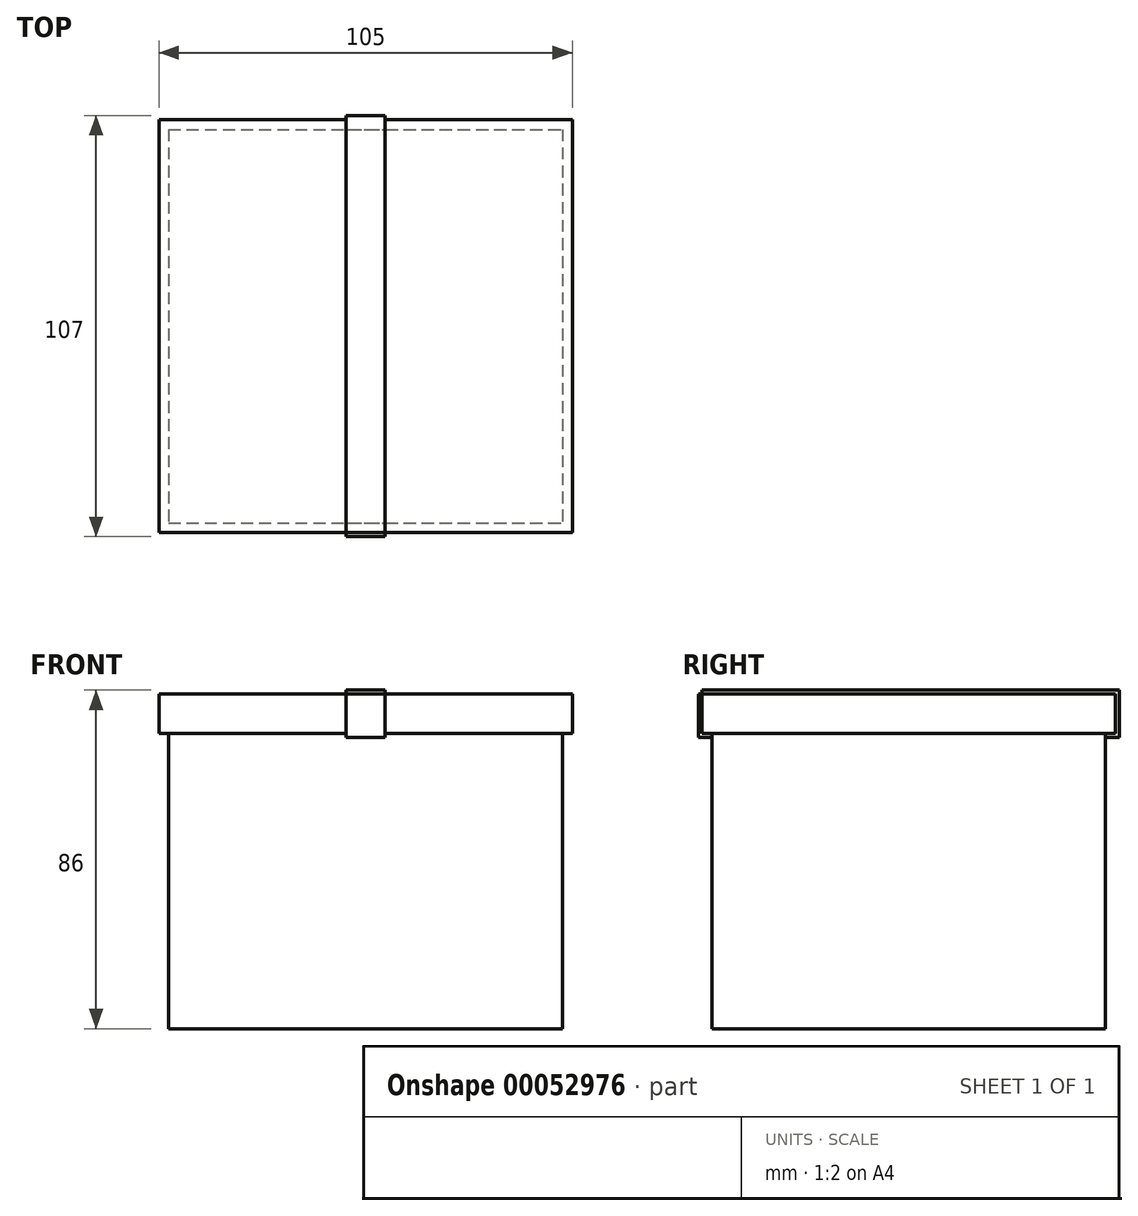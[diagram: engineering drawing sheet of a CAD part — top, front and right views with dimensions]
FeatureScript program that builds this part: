
annotation { "Feature Type Name" : "Feature", "Feature Type Description" : "" }
export const myFeature = defineFeature(function(context is Context, id is Id, definition is map)
    precondition{}
    {
        {
            var Q0;
            Q0=qCreatedBy(makeId("Top.planeOp"),FACE);
            var sketch = newSketch(context, id + "F0", { "sketchPlane" : qUnion([Q0])});
            skLineSegment(sketch, "E0.bottom", {"start": v(-50.02, 49.97) * mm, "end": v(49.98, 49.97) * mm});
            skLineSegment(sketch, "E0.top", {"start": v(-50.02, -50.03) * mm, "end": v(49.98, -50.03) * mm});
            skLineSegment(sketch, "E0.left", {"start": v(-50.02, 49.97) * mm, "end": v(-50.02, -50.03) * mm});
            skLineSegment(sketch, "E0.right", {"start": v(49.98, 49.97) * mm, "end": v(49.98, -50.03) * mm});
            skSolve(sketch);
        }
        {
            var Q0;
            Q0 = qSketchRegion(id + "F0", true);
            var Q1;
            Q1=makeQuery(id+"F0.imprint","IMPRINT",FACE,{"disambiguationData":[TD([[makeQuery(id+"F0.imprint","IMPRINT",EDGE,{"derivedFrom":sQuery(id+"F0.wireOp",EDGE,"E0.bottom")}),-1.0]])]});
            extrude(context, id + "F1", {"entities" : qUnion([Q0, Q1]), "depth" : 75 * mm});
        }
        {
            var Q0;
            Q0=makeQuery(id+"F1.opExtrude","CAP_FACE",FACE,{"disambiguationData":[OSD([sQuery(id+"F0.wireOp",EDGE,"E0.bottom"),sQuery(id+"F0.wireOp",EDGE,"E0.top"),sQuery(id+"F0.wireOp",EDGE,"E0.left"),sQuery(id+"F0.wireOp",EDGE,"E0.right")])],"isStart":false});
            var sketch = newSketch(context, id + "F2", { "sketchPlane" : qUnion([Q0])});
            skLineSegment(sketch, "E1.bottom", {"start": v(0, 0) * mm, "end": v(52.5, 0) * mm});
            skLineSegment(sketch, "E1.top", {"start": v(0, 52.5) * mm, "end": v(52.5, 52.5) * mm});
            skLineSegment(sketch, "E1.left", {"start": v(0, 0) * mm, "end": v(0, 52.5) * mm});
            skLineSegment(sketch, "E1.right", {"start": v(52.5, 0) * mm, "end": v(52.5, 52.5) * mm});
            skLineSegment(sketch, "E2.top", {"start": v(0, -52.5) * mm, "end": v(52.5, -52.5) * mm});
            skLineSegment(sketch, "E2.left", {"start": v(0, 0) * mm, "end": v(0, -52.5) * mm});
            skLineSegment(sketch, "E2.right", {"start": v(52.5, 0) * mm, "end": v(52.5, -52.5) * mm});
            skLineSegment(sketch, "E3.bottom", {"start": v(0, 0) * mm, "end": v(-52.5, 0) * mm});
            skLineSegment(sketch, "E3.top", {"start": v(0, 52.5) * mm, "end": v(-52.5, 52.5) * mm});
            skLineSegment(sketch, "E3.right", {"start": v(-52.5, 0) * mm, "end": v(-52.5, 52.5) * mm});
            skLineSegment(sketch, "E4.top", {"start": v(0, -52.5) * mm, "end": v(-52.5, -52.5) * mm});
            skLineSegment(sketch, "E4.right", {"start": v(-52.5, 0) * mm, "end": v(-52.5, -52.5) * mm});
            skSolve(sketch);
        }
        {
            var Q0;
            Q0 = qSketchRegion(id + "F2", true);
            extrude(context, id + "F3", {"entities" : qUnion([Q0]), "operationType" : NewBodyOperationType.ADD, "depth" : 10 * mm});
        }
        {
            var Q0;
            Q0=makeQuery(id+"F3.opExtrude","CAP_FACE",FACE,{"disambiguationData":[OSD([sQuery(id+"F2.wireOp",EDGE,"E1.top"),sQuery(id+"F2.wireOp",EDGE,"E1.right"),sQuery(id+"F2.wireOp",EDGE,"E2.top"),sQuery(id+"F2.wireOp",EDGE,"E2.right"),sQuery(id+"F2.wireOp",EDGE,"E3.top"),sQuery(id+"F2.wireOp",EDGE,"E3.right"),sQuery(id+"F2.wireOp",EDGE,"E4.top"),sQuery(id+"F2.wireOp",EDGE,"E4.right")])],"isStart":false});
            var sketch = newSketch(context, id + "F4", { "sketchPlane" : qUnion([Q0])});
            skLineSegment(sketch, "E5.bottom", {"start": v(0, 0) * mm, "end": v(-5, 0) * mm});
            skLineSegment(sketch, "E5.top", {"start": v(0, 52.5) * mm, "end": v(-5, 52.5) * mm});
            skLineSegment(sketch, "E5.left", {"start": v(0, 0) * mm, "end": v(0, 52.5) * mm});
            skLineSegment(sketch, "E5.right", {"start": v(-5, 0) * mm, "end": v(-5, 52.5) * mm});
            skLineSegment(sketch, "E6.top", {"start": v(0, -52.5) * mm, "end": v(-5, -52.5) * mm});
            skLineSegment(sketch, "E6.left", {"start": v(0, 0) * mm, "end": v(0, -52.5) * mm});
            skLineSegment(sketch, "E6.right", {"start": v(-5, 0) * mm, "end": v(-5, -52.5) * mm});
            skLineSegment(sketch, "E7.bottom", {"start": v(0, 0) * mm, "end": v(5, 0) * mm});
            skLineSegment(sketch, "E7.top", {"start": v(0, -52.5) * mm, "end": v(5, -52.5) * mm});
            skLineSegment(sketch, "E7.right", {"start": v(5, 0) * mm, "end": v(5, -52.5) * mm});
            skLineSegment(sketch, "E8.top", {"start": v(0, 52.5) * mm, "end": v(5, 52.5) * mm});
            skLineSegment(sketch, "E8.right", {"start": v(5, 0) * mm, "end": v(5, 52.5) * mm});
            skSolve(sketch);
        }
        {
            var Q0;
            Q0 = qSketchRegion(id + "F4", true);
            extrude(context, id + "F5", {"entities" : qUnion([Q0]), "operationType" : NewBodyOperationType.ADD, "depth" : 1 * mm});
        }
        {
            var Q0;
            Q0=makeQuery(id+"F5.boolean.opBoolean","MERGE",FACE,{"derivedFrom":[makeQuery(id+"F3.opExtrude","SWEPT_FACE",FACE,{"disambiguationData":[OSD([sQuery(id+"F2.wireOp",EDGE,"E2.top"),sQuery(id+"F2.wireOp",EDGE,"E4.top")])]}),makeQuery(id+"F5.opExtrude","SWEPT_FACE",FACE,{"disambiguationData":[OSD([sQuery(id+"F4.wireOp",EDGE,"E6.top"),sQuery(id+"F4.wireOp",EDGE,"E7.top")])]})]});
            var sketch = newSketch(context, id + "F6", { "sketchPlane" : qUnion([Q0])});
            skLineSegment(sketch, "E9.bottom", {"start": v(-5, 85) * mm, "end": v(5, 85) * mm});
            skLineSegment(sketch, "E9.top", {"start": v(-5, 75) * mm, "end": v(5, 75) * mm});
            skLineSegment(sketch, "E9.left", {"start": v(-5, 85) * mm, "end": v(-5, 75) * mm});
            skLineSegment(sketch, "E9.right", {"start": v(5, 85) * mm, "end": v(5, 75) * mm});
            skSolve(sketch);
        }
        {
            var Q0;
            Q0 = qSketchRegion(id + "F6", true);
            extrude(context, id + "F7", {"entities" : qUnion([Q0]), "operationType" : NewBodyOperationType.ADD, "depth" : 1 * mm});
        }
        {
            var Q0;
            Q0=makeQuery(id+"F5.boolean.opBoolean","MERGE",FACE,{"derivedFrom":[makeQuery(id+"F3.opExtrude","SWEPT_FACE",FACE,{"disambiguationData":[OSD([sQuery(id+"F2.wireOp",EDGE,"E1.top"),sQuery(id+"F2.wireOp",EDGE,"E3.top")])]}),makeQuery(id+"F5.opExtrude","SWEPT_FACE",FACE,{"disambiguationData":[OSD([sQuery(id+"F4.wireOp",EDGE,"E5.top"),sQuery(id+"F4.wireOp",EDGE,"E8.top")])]})]});
            var sketch = newSketch(context, id + "F8", { "sketchPlane" : qUnion([Q0])});
            skLineSegment(sketch, "E10.bottom", {"start": v(5, 86) * mm, "end": v(-5, 86) * mm});
            skLineSegment(sketch, "E10.top", {"start": v(5, 75) * mm, "end": v(-5, 75) * mm});
            skLineSegment(sketch, "E10.left", {"start": v(5, 86) * mm, "end": v(5, 75) * mm});
            skLineSegment(sketch, "E10.right", {"start": v(-5, 86) * mm, "end": v(-5, 75) * mm});
            skSolve(sketch);
        }
        {
            var Q0;
            Q0 = qSketchRegion(id + "F8", true);
            extrude(context, id + "F9", {"entities" : qUnion([Q0]), "operationType" : NewBodyOperationType.ADD, "depth" : 1 * mm});
        }
        {
            var Q0;
            Q0=makeQuery(id+"F9.boolean.opBoolean","MERGE",FACE,{"derivedFrom":[makeQuery(id+"F7.boolean.opBoolean","MERGE",FACE,{"derivedFrom":[makeQuery(id+"F3.opExtrude","CAP_FACE",FACE,{"disambiguationData":[OSD([sQuery(id+"F2.wireOp",EDGE,"E1.top"),sQuery(id+"F2.wireOp",EDGE,"E1.right"),sQuery(id+"F2.wireOp",EDGE,"E2.top"),sQuery(id+"F2.wireOp",EDGE,"E2.right"),sQuery(id+"F2.wireOp",EDGE,"E3.top"),sQuery(id+"F2.wireOp",EDGE,"E3.right"),sQuery(id+"F2.wireOp",EDGE,"E4.top"),sQuery(id+"F2.wireOp",EDGE,"E4.right")])],"isStart":true}),makeQuery(id+"F7.opExtrude","SWEPT_FACE",FACE,{"disambiguationData":[OSD([sQuery(id+"F6.wireOp",EDGE,"E9.top")])]})]}),makeQuery(id+"F9.opExtrude","SWEPT_FACE",FACE,{"disambiguationData":[OSD([sQuery(id+"F8.wireOp",EDGE,"E10.top")])]})]});
            var sketch = newSketch(context, id + "F10", { "sketchPlane" : qUnion([Q0])});
            skLineSegment(sketch, "E11.bottom", {"start": v(-5, 53.5) * mm, "end": v(5, 53.5) * mm});
            skLineSegment(sketch, "E11.top", {"start": v(-5, 50.03) * mm, "end": v(5, 50.03) * mm});
            skLineSegment(sketch, "E11.left", {"start": v(-5, 53.5) * mm, "end": v(-5, 50.03) * mm});
            skLineSegment(sketch, "E11.right", {"start": v(5, 53.5) * mm, "end": v(5, 50.03) * mm});
            skSolve(sketch);
        }
        {
            var Q0;
            Q0 = qSketchRegion(id + "F10", true);
            extrude(context, id + "F11", {"entities" : qUnion([Q0]), "operationType" : NewBodyOperationType.ADD, "depth" : 1 * mm});
        }
        {
            var Q0;
            Q0=makeQuery(id+"F9.boolean.opBoolean","MERGE",FACE,{"derivedFrom":[makeQuery(id+"F7.boolean.opBoolean","MERGE",FACE,{"derivedFrom":[makeQuery(id+"F3.opExtrude","CAP_FACE",FACE,{"disambiguationData":[OSD([sQuery(id+"F2.wireOp",EDGE,"E1.top"),sQuery(id+"F2.wireOp",EDGE,"E1.right"),sQuery(id+"F2.wireOp",EDGE,"E2.top"),sQuery(id+"F2.wireOp",EDGE,"E2.right"),sQuery(id+"F2.wireOp",EDGE,"E3.top"),sQuery(id+"F2.wireOp",EDGE,"E3.right"),sQuery(id+"F2.wireOp",EDGE,"E4.top"),sQuery(id+"F2.wireOp",EDGE,"E4.right")])],"isStart":true}),makeQuery(id+"F7.opExtrude","SWEPT_FACE",FACE,{"disambiguationData":[OSD([sQuery(id+"F6.wireOp",EDGE,"E9.top")])]})]}),makeQuery(id+"F9.opExtrude","SWEPT_FACE",FACE,{"disambiguationData":[OSD([sQuery(id+"F8.wireOp",EDGE,"E10.top")])]})]});
            var sketch = newSketch(context, id + "F12", { "sketchPlane" : qUnion([Q0])});
            skLineSegment(sketch, "E12.bottom", {"start": v(-5, -49.97) * mm, "end": v(5, -49.97) * mm});
            skLineSegment(sketch, "E12.top", {"start": v(-5, -53.5) * mm, "end": v(5, -53.5) * mm});
            skLineSegment(sketch, "E12.left", {"start": v(-5, -49.97) * mm, "end": v(-5, -53.5) * mm});
            skLineSegment(sketch, "E12.right", {"start": v(5, -49.97) * mm, "end": v(5, -53.5) * mm});
            skSolve(sketch);
        }
        {
            var Q0;
            Q0 = qSketchRegion(id + "F12", true);
            extrude(context, id + "F13", {"entities" : qUnion([Q0]), "operationType" : NewBodyOperationType.ADD, "depth" : 1 * mm});
        }
    });
